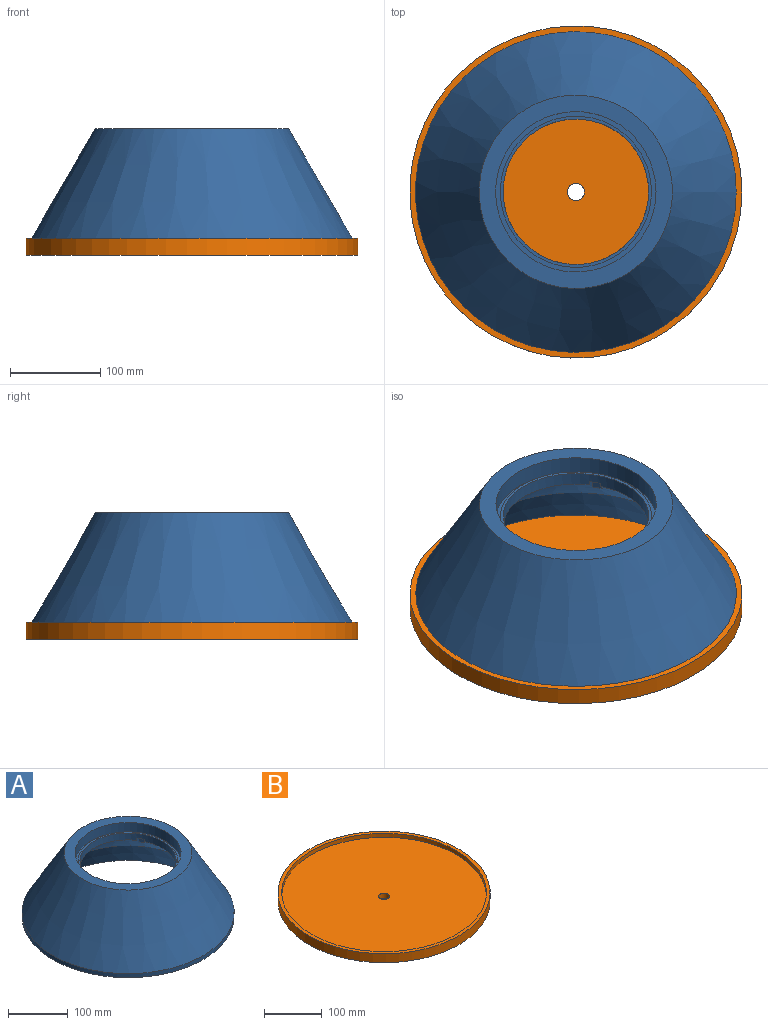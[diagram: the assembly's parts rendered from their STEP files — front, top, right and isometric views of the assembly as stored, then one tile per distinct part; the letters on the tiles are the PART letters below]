
ASSEMBLY  parts=2 mates=1
PART A: 23 faces, bbox 355.7x355.7x130 mm
  f0: cone r=133.01mm half-angle=47.1deg, axis (0,0,-1), area 47316.9mm2, adj f1,f9,f12,f13,f14,f16,f17,f18
  f1: cylinder r=80.64mm len=161.29mm, axis (0,0,1), area 7034.3mm2, adj f0,f10,f11,f12,f13,f15,f16,f17
  f2: cylinder r=83.82mm len=167.64mm, axis (0,0,1), area 2244.8mm2, adj f3,f10
  f3: plane 177.8x177.8mm, normal (0,0,1), area 2756.5mm2, adj f2,f4
  f4: cylinder r=88.9mm len=177.8mm, axis (0,0,1), area 11066mm2, adj f3,f5
  f5: plane 214.37x214.37mm, normal (0,0,1), area 11262.5mm2, adj f4,f6
  f6: cone r=107.18mm half-angle=30.1deg, axis (0,0,-1), area 125960.8mm2, adj f5,f7
  f7: cylinder r=177.8mm len=355.6mm, axis (0,0,1), area 9222.1mm2, adj f6,f8
  f8: plane 355.6x355.6mm, normal (0,0,-1), area 15892.4mm2, adj f7,f9
  f9: cone r=162.95mm half-angle=30.1deg, axis (0,0,-1), area 55464.5mm2, adj f0,f8
  f10: plane 167.64x167.64mm, normal (0,0,1), area 1640.5mm2, adj f1,f2
  f11: plane 17.16x17.02mm, normal (0,0,-1), area 154.3mm2, adj f1,f12,f13,f14
  f12: plane 15.82x10.73mm, normal (0.5,-0.87,0), area 123.8mm2, adj f0,f1,f11,f14
  f13: plane 15.82x10.73mm, normal (-0.5,0.87,0), area 123.8mm2, adj f0,f1,f11,f14
  f14: plane 15.75x11mm, normal (-0.87,-0.5,0), area 198.4mm2, adj f0,f11,f12,f13
  f15: plane 17.16x17.02mm, normal (0,0,-1), area 154.3mm2, adj f1,f16,f17,f18
  f16: plane 15.82x10.73mm, normal (0.5,0.87,0), area 123.8mm2, adj f0,f1,f15,f18
  f17: plane 15.82x10.73mm, normal (-0.5,-0.87,0), area 123.8mm2, adj f0,f1,f15,f18
  f18: plane 15.75x11mm, normal (0.87,-0.5,0), area 198.4mm2, adj f0,f15,f16,f17
  f19: plane 12.7x12.32mm, normal (0,0,-1), area 154.3mm2, adj f1,f20,f21,f22
  f20: plane 15.82x12.38mm, normal (-1,0,0), area 123.8mm2, adj f0,f1,f19,f22
  f21: plane 15.82x12.38mm, normal (1,0,0), area 123.8mm2, adj f0,f1,f19,f22
  f22: plane 15.77x12.73mm, normal (0,1,0), area 198.4mm2, adj f0,f19,f20,f21
PART B: 6 faces, bbox 368.3x368.3x19.1 mm
  f0: cylinder r=184.15mm len=368.3mm, axis (0,0,-1), area 22041.8mm2, adj f1,f2
  f1: plane 368.3x368.3mm, normal (0,0,1), area 7220.6mm2, adj f0,f3
  f2: plane 368.3x368.3mm, normal (0,0,-1), area 106250.2mm2, adj f0,f5
  f3: cylinder r=177.8mm len=355.6mm, axis (0,0,1), area 9222.1mm2, adj f1,f4
  f4: plane 355.6x355.6mm, normal (0,0,1), area 99029.6mm2, adj f3,f5
  f5: cylinder r=9.53mm len=19.05mm, axis (0,0,1), area 646.1mm2, adj f2,f4
PLACE A t=(-0.02,0.04,96.99)mm
PLACE B t=(-0.02,0.04,-9.45)mm
MATE fastened A.f0 <-> B.f3  axis (0,0,-1) through (-0.02,0.04,1.34)mm
